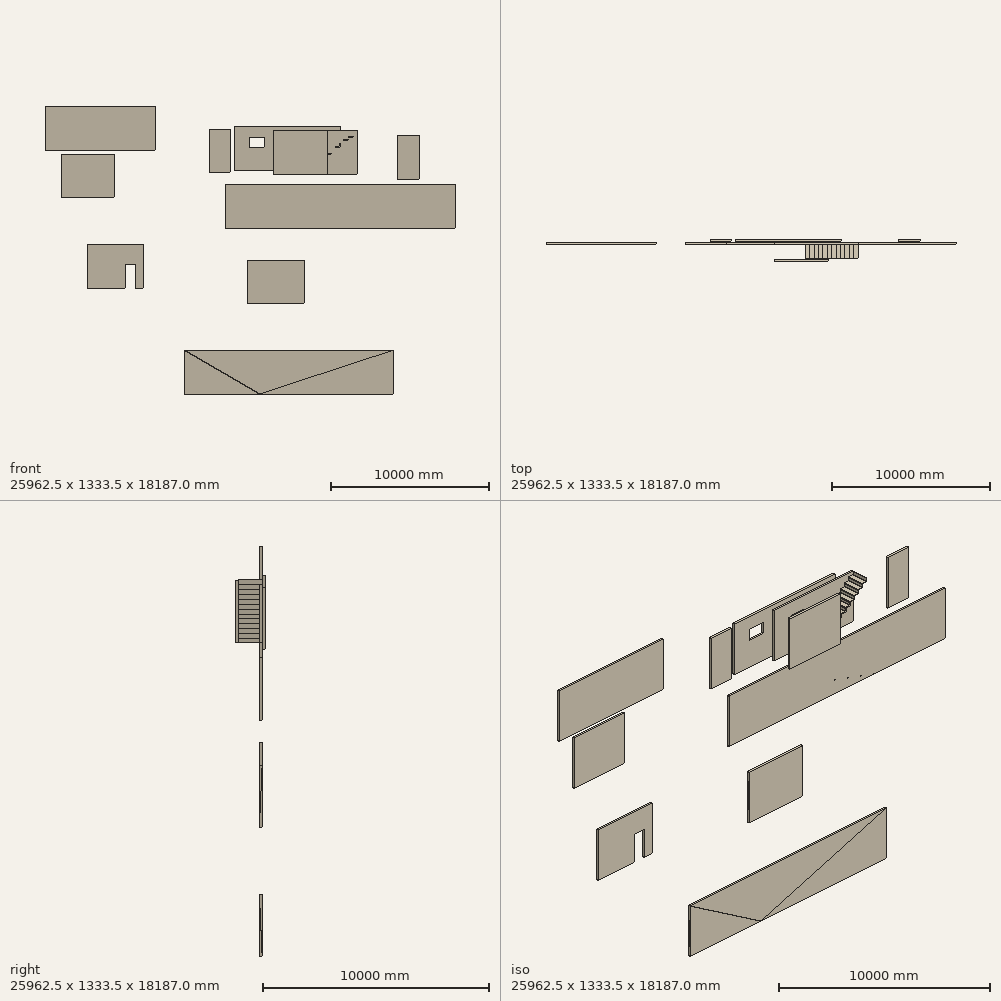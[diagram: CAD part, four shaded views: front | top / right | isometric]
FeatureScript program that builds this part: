
annotation { "Feature Type Name" : "Feature", "Feature Type Description" : "" }
export const myFeature = defineFeature(function(context is Context, id is Id, definition is map)
    precondition{}
    {
        {
            var Q0;
            Q0=qCreatedBy(makeId("Front.planeOp"),FACE);
            var sketch = newSketch(context, id + "F0", { "sketchPlane" : qUnion([Q0])});
            skLineSegment(sketch, "E0", {"start": v(2395.88, -99.39) * mm, "end": v(2414.93, -99.39) * mm});
            skLineSegment(sketch, "E1", {"start": v(2395.88, -99.39) * mm, "end": v(2395.88, -277.19) * mm});
            skLineSegment(sketch, "E2.bottom", {"start": v(2395.88, -277.19) * mm, "end": v(2097.43, -277.19) * mm});
            skLineSegment(sketch, "E2.top", {"start": v(2280.9, -315.29) * mm, "end": v(2135.53, -315.29) * mm});
            skLineSegment(sketch, "E2.right", {"start": v(2097.43, -277.19) * mm, "end": v(2097.43, -315.29) * mm});
            skLineSegment(sketch, "E3", {"start": v(2414.93, -99.39) * mm, "end": v(2414.93, -315.29) * mm});
            skLineSegment(sketch, "E4", {"start": v(2414.93, -315.29) * mm, "end": v(2280.9, -315.29) * mm});
            skLineSegment(sketch, "E5", {"start": v(1837.08, -531.19) * mm, "end": v(1837.08, -708.99) * mm});
            skLineSegment(sketch, "E6.bottom", {"start": v(1837.08, -708.99) * mm, "end": v(1538.63, -708.99) * mm});
            skLineSegment(sketch, "E6.top", {"start": v(1805.95, -747.09) * mm, "end": v(1576.73, -747.09) * mm});
            skLineSegment(sketch, "E6.right", {"start": v(1538.63, -708.99) * mm, "end": v(1538.63, -747.09) * mm});
            skLineSegment(sketch, "E7", {"start": v(1856.13, -531.19) * mm, "end": v(1856.13, -747.09) * mm});
            skLineSegment(sketch, "E8", {"start": v(1856.13, -747.09) * mm, "end": v(1805.95, -747.09) * mm});
            skLineSegment(sketch, "E9", {"start": v(2116.48, -315.29) * mm, "end": v(2116.48, -493.09) * mm});
            skLineSegment(sketch, "E10.bottom", {"start": v(2116.48, -493.09) * mm, "end": v(1818.03, -493.09) * mm});
            skLineSegment(sketch, "E10.top", {"start": v(2135.53, -531.19) * mm, "end": v(1856.13, -531.19) * mm});
            skLineSegment(sketch, "E10.right", {"start": v(1818.03, -493.09) * mm, "end": v(1818.03, -531.19) * mm});
            skLineSegment(sketch, "E11", {"start": v(2135.53, -315.29) * mm, "end": v(2135.53, -531.19) * mm});
            skLineSegment(sketch, "E12", {"start": v(998.88, -1178.89) * mm, "end": v(998.88, -1356.69) * mm});
            skLineSegment(sketch, "E13.bottom", {"start": v(998.88, -1356.69) * mm, "end": v(700.43, -1356.69) * mm});
            skLineSegment(sketch, "E13.top", {"start": v(1017.93, -1394.79) * mm, "end": v(738.53, -1394.79) * mm});
            skLineSegment(sketch, "E13.right", {"start": v(700.43, -1356.69) * mm, "end": v(700.43, -1394.79) * mm});
            skLineSegment(sketch, "E14", {"start": v(1017.93, -1178.89) * mm, "end": v(1017.93, -1394.79) * mm});
            skLineSegment(sketch, "E15", {"start": v(1557.68, -747.09) * mm, "end": v(1557.68, -924.89) * mm});
            skLineSegment(sketch, "E16.bottom", {"start": v(1557.68, -924.89) * mm, "end": v(1259.23, -924.89) * mm});
            skLineSegment(sketch, "E16.top", {"start": v(1557.68, -962.99) * mm, "end": v(1297.33, -962.99) * mm});
            skLineSegment(sketch, "E16.right", {"start": v(1259.23, -924.89) * mm, "end": v(1259.23, -962.99) * mm});
            skLineSegment(sketch, "E17", {"start": v(1576.73, -747.09) * mm, "end": v(1576.73, -962.99) * mm});
            skLineSegment(sketch, "E18", {"start": v(1576.73, -962.99) * mm, "end": v(1557.68, -962.99) * mm});
            skLineSegment(sketch, "E19", {"start": v(1278.28, -962.99) * mm, "end": v(1278.28, -1140.79) * mm});
            skLineSegment(sketch, "E20.bottom", {"start": v(1278.28, -1140.79) * mm, "end": v(979.83, -1140.79) * mm});
            skLineSegment(sketch, "E20.right", {"start": v(979.83, -1140.79) * mm, "end": v(979.83, -1178.89) * mm});
            skLineSegment(sketch, "E21", {"start": v(1297.33, -962.99) * mm, "end": v(1297.33, -1178.89) * mm});
            skLineSegment(sketch, "E22", {"start": v(1297.33, -1178.89) * mm, "end": v(1017.93, -1178.89) * mm});
            skLineSegment(sketch, "E23.bottom", {"start": v(2414.93, -99.39) * mm, "end": v(-2893.67, -99.39) * mm});
            skLineSegment(sketch, "E23.top", {"start": v(2414.93, -2867.99) * mm, "end": v(-2893.67, -2867.99) * mm});
            skLineSegment(sketch, "E23.left", {"start": v(2414.93, -99.39) * mm, "end": v(2414.93, -2867.99) * mm});
            skLineSegment(sketch, "E23.right", {"start": v(-2893.67, -99.39) * mm, "end": v(-2893.67, -2867.99) * mm});
            skLineSegment(sketch, "E24", {"start": v(719.48, -1394.79) * mm, "end": v(719.48, -1572.59) * mm});
            skLineSegment(sketch, "E25.bottom", {"start": v(719.48, -1572.59) * mm, "end": v(421.03, -1572.59) * mm});
            skLineSegment(sketch, "E25.right", {"start": v(421.03, -1572.59) * mm, "end": v(421.03, -1610.69) * mm});
            skLineSegment(sketch, "E26", {"start": v(738.53, -1394.79) * mm, "end": v(738.53, -1610.69) * mm});
            skLineSegment(sketch, "E27", {"start": v(738.53, -1610.69) * mm, "end": v(459.13, -1610.69) * mm});
            skLineSegment(sketch, "E28", {"start": v(160.68, -1826.59) * mm, "end": v(160.68, -2004.39) * mm});
            skLineSegment(sketch, "E29.bottom", {"start": v(160.68, -2004.39) * mm, "end": v(-137.77, -2004.39) * mm});
            skLineSegment(sketch, "E29.top", {"start": v(160.68, -2042.49) * mm, "end": v(-99.67, -2042.49) * mm});
            skLineSegment(sketch, "E29.right", {"start": v(-137.77, -2004.39) * mm, "end": v(-137.77, -2042.49) * mm});
            skLineSegment(sketch, "E30", {"start": v(179.73, -1826.59) * mm, "end": v(179.73, -2042.49) * mm});
            skLineSegment(sketch, "E31", {"start": v(179.73, -2042.49) * mm, "end": v(160.68, -2042.49) * mm});
            skLineSegment(sketch, "E32", {"start": v(440.08, -1610.69) * mm, "end": v(440.08, -1788.49) * mm});
            skLineSegment(sketch, "E33.bottom", {"start": v(440.08, -1788.49) * mm, "end": v(141.63, -1788.49) * mm});
            skLineSegment(sketch, "E33.top", {"start": v(440.08, -1826.59) * mm, "end": v(179.73, -1826.59) * mm});
            skLineSegment(sketch, "E33.right", {"start": v(141.63, -1788.49) * mm, "end": v(141.63, -1826.59) * mm});
            skLineSegment(sketch, "E34", {"start": v(459.13, -1610.69) * mm, "end": v(459.13, -1826.59) * mm});
            skLineSegment(sketch, "E35", {"start": v(459.13, -1826.59) * mm, "end": v(440.08, -1826.59) * mm});
            skLineSegment(sketch, "E36", {"start": v(-118.72, -2042.49) * mm, "end": v(-118.72, -2220.29) * mm});
            skLineSegment(sketch, "E37.bottom", {"start": v(-118.72, -2220.29) * mm, "end": v(-417.17, -2220.29) * mm});
            skLineSegment(sketch, "E37.right", {"start": v(-417.17, -2220.29) * mm, "end": v(-417.17, -2258.39) * mm});
            skLineSegment(sketch, "E38", {"start": v(-99.67, -2042.49) * mm, "end": v(-99.67, -2258.39) * mm});
            skLineSegment(sketch, "E39", {"start": v(-99.67, -2258.39) * mm, "end": v(-379.07, -2258.39) * mm});
            skLineSegment(sketch, "E40", {"start": v(-398.12, -2258.39) * mm, "end": v(-398.12, -2436.19) * mm});
            skLineSegment(sketch, "E41.bottom", {"start": v(-398.12, -2436.19) * mm, "end": v(-696.57, -2436.19) * mm});
            skLineSegment(sketch, "E41.right", {"start": v(-696.57, -2436.19) * mm, "end": v(-696.57, -2474.29) * mm});
            skLineSegment(sketch, "E42", {"start": v(-379.07, -2258.39) * mm, "end": v(-379.07, -2474.29) * mm});
            skLineSegment(sketch, "E43", {"start": v(-379.07, -2474.29) * mm, "end": v(-658.47, -2474.29) * mm});
            skLineSegment(sketch, "E44", {"start": v(-677.52, -2474.29) * mm, "end": v(-677.52, -2652.09) * mm});
            skLineSegment(sketch, "E45.bottom", {"start": v(-677.52, -2652.09) * mm, "end": v(-975.97, -2652.09) * mm});
            skLineSegment(sketch, "E45.right", {"start": v(-975.97, -2652.09) * mm, "end": v(-975.97, -2690.19) * mm});
            skLineSegment(sketch, "E46", {"start": v(-658.47, -2474.29) * mm, "end": v(-658.47, -2690.19) * mm});
            skLineSegment(sketch, "E47", {"start": v(-658.47, -2690.19) * mm, "end": v(-937.87, -2690.19) * mm});
            skLineSegment(sketch, "E48.top", {"start": v(-956.92, -2867.99) * mm, "end": v(-937.87, -2867.99) * mm});
            skLineSegment(sketch, "E48.left", {"start": v(-956.92, -2690.19) * mm, "end": v(-956.92, -2867.99) * mm});
            skLineSegment(sketch, "E48.right", {"start": v(-937.87, -2690.19) * mm, "end": v(-937.87, -2867.99) * mm});
            skLineSegment(sketch, "E49.trimOffspring", {"start": v(2116.48, -315.29) * mm, "end": v(2097.43, -315.29) * mm});
            skLineSegment(sketch, "E50.trimOffspring", {"start": v(1837.08, -531.19) * mm, "end": v(1818.03, -531.19) * mm});
            skLineSegment(sketch, "E51.trimOffspring", {"start": v(1557.68, -747.09) * mm, "end": v(1538.63, -747.09) * mm});
            skLineSegment(sketch, "E52.trimOffspring", {"start": v(1278.28, -962.99) * mm, "end": v(1259.23, -962.99) * mm});
            skLineSegment(sketch, "E53.trimOffspring", {"start": v(998.88, -1178.89) * mm, "end": v(979.83, -1178.89) * mm});
            skLineSegment(sketch, "E54.trimOffspring", {"start": v(719.48, -1394.79) * mm, "end": v(700.43, -1394.79) * mm});
            skLineSegment(sketch, "E55.trimOffspring", {"start": v(440.08, -1610.69) * mm, "end": v(421.03, -1610.69) * mm});
            skLineSegment(sketch, "E56.trimOffspring", {"start": v(160.68, -1826.59) * mm, "end": v(141.63, -1826.59) * mm});
            skLineSegment(sketch, "E57.trimOffspring", {"start": v(-118.72, -2042.49) * mm, "end": v(-137.77, -2042.49) * mm});
            skLineSegment(sketch, "E58.trimOffspring", {"start": v(-398.12, -2258.39) * mm, "end": v(-417.17, -2258.39) * mm});
            skLineSegment(sketch, "E59.trimOffspring", {"start": v(-677.52, -2474.29) * mm, "end": v(-696.57, -2474.29) * mm});
            skLineSegment(sketch, "E60.trimOffspring", {"start": v(-956.92, -2690.19) * mm, "end": v(-975.97, -2690.19) * mm});
            skLineSegment(sketch, "E61.bottom", {"start": v(-1772.9, -816.92) * mm, "end": v(-963.27, -816.92) * mm});
            skLineSegment(sketch, "E61.top", {"start": v(-1772.9, -1394.79) * mm, "end": v(-963.27, -1394.79) * mm});
            skLineSegment(sketch, "E61.left", {"start": v(-1772.9, -816.92) * mm, "end": v(-1772.9, -1394.79) * mm});
            skLineSegment(sketch, "E61.right", {"start": v(-963.27, -816.92) * mm, "end": v(-963.27, -1394.79) * mm});
            skLineSegment(sketch, "E62.bottom", {"start": v(-984.42, -11080.12) * mm, "end": v(-4578.52, -11080.12) * mm});
            skLineSegment(sketch, "E62.top", {"start": v(-984.42, -8311.52) * mm, "end": v(-4578.52, -8311.52) * mm});
            skLineSegment(sketch, "E62.left", {"start": v(-984.42, -11080.12) * mm, "end": v(-984.42, -8311.52) * mm});
            skLineSegment(sketch, "E62.right", {"start": v(-4578.52, -11080.12) * mm, "end": v(-4578.52, -8311.52) * mm});
            skPoint(sketch, "E62.middle", {"position": v(-2781.47, -9695.82) * mm});
            skLineSegment(sketch, "E63.bottom", {"start": v(8601.23, -6325.37) * mm, "end": v(-5942.68, -6325.37) * mm});
            skLineSegment(sketch, "E63.top", {"start": v(8601.23, -3556.77) * mm, "end": v(-5942.68, -3556.77) * mm});
            skLineSegment(sketch, "E63.left", {"start": v(8601.23, -6325.37) * mm, "end": v(8601.23, -3556.77) * mm});
            skLineSegment(sketch, "E63.right", {"start": v(-5942.68, -6325.37) * mm, "end": v(-5942.68, -3556.77) * mm});
            skPoint(sketch, "E63.middle", {"position": v(1329.27, -4941.07) * mm});
            skLineSegment(sketch, "E64.bottom", {"start": v(4653.66, -16802.72) * mm, "end": v(-8547.23, -16802.72) * mm});
            skLineSegment(sketch, "E64.top", {"start": v(4653.66, -14034.12) * mm, "end": v(-8547.23, -14034.12) * mm});
            skLineSegment(sketch, "E64.left", {"start": v(4653.66, -16802.72) * mm, "end": v(4653.66, -14034.12) * mm});
            skLineSegment(sketch, "E64.right", {"start": v(-8547.23, -16802.72) * mm, "end": v(-8547.23, -14034.12) * mm});
            skPoint(sketch, "E64.middle", {"position": v(-1946.79, -15418.42) * mm});
            skLineSegment(sketch, "E65.bottom", {"start": v(-11136.45, -10094.37) * mm, "end": v(-14730.55, -10094.37) * mm});
            skLineSegment(sketch, "E65.top", {"start": v(-11136.45, -7325.77) * mm, "end": v(-14730.55, -7325.77) * mm});
            skLineSegment(sketch, "E65.left", {"start": v(-11136.45, -10094.37) * mm, "end": v(-11136.45, -7325.77) * mm});
            skLineSegment(sketch, "E65.right", {"start": v(-14730.55, -10094.37) * mm, "end": v(-14730.55, -7325.77) * mm});
            skPoint(sketch, "E65.middle", {"position": v(-12933.5, -8710.07) * mm});
            skLineSegment(sketch, "E66.bottom", {"start": v(-10369.88, -1384.3) * mm, "end": v(-17361.23, -1384.3) * mm});
            skLineSegment(sketch, "E66.top", {"start": v(-10369.88, 1384.3) * mm, "end": v(-17361.23, 1384.3) * mm});
            skLineSegment(sketch, "E66.left", {"start": v(-10369.88, -1384.3) * mm, "end": v(-10369.88, 1384.3) * mm});
            skLineSegment(sketch, "E66.right", {"start": v(-17361.23, -1384.3) * mm, "end": v(-17361.23, 1384.3) * mm});
            skPoint(sketch, "E66.middle", {"position": v(-13865.56, 0) * mm});
            skLineSegment(sketch, "E67.bottom", {"start": v(-12994.75, -4376.62) * mm, "end": v(-16357.07, -4376.62) * mm});
            skLineSegment(sketch, "E67.top", {"start": v(-12994.75, -1608.02) * mm, "end": v(-16357.07, -1608.02) * mm});
            skLineSegment(sketch, "E67.left", {"start": v(-12994.75, -4376.62) * mm, "end": v(-12994.75, -1608.02) * mm});
            skLineSegment(sketch, "E67.right", {"start": v(-16357.07, -4376.62) * mm, "end": v(-16357.07, -1608.02) * mm});
            skPoint(sketch, "E67.middle", {"position": v(-14675.91, -2992.32) * mm});
            skCircle(sketch, "E68", {"center": v(-3794.26, -16802.72) * mm, "radius": 3.18 * mm});
            skCircle(sketch, "E69", {"center": v(3848.26, -6325.37) * mm, "radius": 3.18 * mm});
            skLineSegment(sketch, "E70.bottom", {"start": v(-14047.12, -10094.37) * mm, "end": v(-13449.67, -10094.37) * mm});
            skLineSegment(sketch, "E71.bottom", {"start": v(-11648.33, -10094.37) * mm, "end": v(-12317.56, -10094.37) * mm});
            skLineSegment(sketch, "E71.top", {"start": v(-11648.33, -8564.93) * mm, "end": v(-12317.56, -8564.93) * mm});
            skLineSegment(sketch, "E71.left", {"start": v(-11648.33, -10094.37) * mm, "end": v(-11648.33, -8564.93) * mm});
            skLineSegment(sketch, "E71.right", {"start": v(-12317.56, -10094.37) * mm, "end": v(-12317.56, -8564.93) * mm});
            skSolve(sketch);
        }
        {
            var Q0;
            Q0=makeQuery(id+"F0.imprint","IMPRINT",FACE,{"disambiguationData":[TD([[makeQuery(id+"F0.imprint","IMPRINT",EDGE,{"derivedFrom":sQuery(id+"F0.wireOp",EDGE,"E0")}),-1.0]])]});
            extrude(context, id + "F1", {"entities" : qUnion([Q0]), "depth" : 1035.05 * mm, "offsetDistance" : 25.4 * mm});
        }
        {
            var Q0;
            Q0=makeQuery(id+"F1.opExtrude","CAP_FACE",FACE,{"disambiguationData":[OSD([sQuery(id+"F0.wireOp",EDGE,"E0"),sQuery(id+"F0.wireOp",EDGE,"E1"),sQuery(id+"F0.wireOp",EDGE,"E2.bottom"),sQuery(id+"F0.wireOp",EDGE,"E2.top"),sQuery(id+"F0.wireOp",EDGE,"E2.right"),sQuery(id+"F0.wireOp",EDGE,"E3"),sQuery(id+"F0.wireOp",EDGE,"E4"),sQuery(id+"F0.wireOp",EDGE,"E5"),sQuery(id+"F0.wireOp",EDGE,"E6.bottom"),sQuery(id+"F0.wireOp",EDGE,"E6.top"),sQuery(id+"F0.wireOp",EDGE,"E6.right"),sQuery(id+"F0.wireOp",EDGE,"E7"),sQuery(id+"F0.wireOp",EDGE,"E8"),sQuery(id+"F0.wireOp",EDGE,"E9"),sQuery(id+"F0.wireOp",EDGE,"E10.bottom"),sQuery(id+"F0.wireOp",EDGE,"E10.top"),sQuery(id+"F0.wireOp",EDGE,"E10.right"),sQuery(id+"F0.wireOp",EDGE,"E11"),sQuery(id+"F0.wireOp",EDGE,"E12"),sQuery(id+"F0.wireOp",EDGE,"E13.bottom"),sQuery(id+"F0.wireOp",EDGE,"E13.top"),sQuery(id+"F0.wireOp",EDGE,"E13.right"),sQuery(id+"F0.wireOp",EDGE,"E14"),sQuery(id+"F0.wireOp",EDGE,"E15"),sQuery(id+"F0.wireOp",EDGE,"E16.bottom"),sQuery(id+"F0.wireOp",EDGE,"E16.top"),sQuery(id+"F0.wireOp",EDGE,"E16.right"),sQuery(id+"F0.wireOp",EDGE,"E17"),sQuery(id+"F0.wireOp",EDGE,"E18"),sQuery(id+"F0.wireOp",EDGE,"E19"),sQuery(id+"F0.wireOp",EDGE,"E20.bottom"),sQuery(id+"F0.wireOp",EDGE,"E20.right"),sQuery(id+"F0.wireOp",EDGE,"E21"),sQuery(id+"F0.wireOp",EDGE,"E22"),sQuery(id+"F0.wireOp",EDGE,"E23.top"),sQuery(id+"F0.wireOp",EDGE,"E24"),sQuery(id+"F0.wireOp",EDGE,"E25.bottom"),sQuery(id+"F0.wireOp",EDGE,"E25.right"),sQuery(id+"F0.wireOp",EDGE,"E26"),sQuery(id+"F0.wireOp",EDGE,"E27"),sQuery(id+"F0.wireOp",EDGE,"E28"),sQuery(id+"F0.wireOp",EDGE,"E29.bottom"),sQuery(id+"F0.wireOp",EDGE,"E29.top"),sQuery(id+"F0.wireOp",EDGE,"E29.right"),sQuery(id+"F0.wireOp",EDGE,"E30"),sQuery(id+"F0.wireOp",EDGE,"E31"),sQuery(id+"F0.wireOp",EDGE,"E32"),sQuery(id+"F0.wireOp",EDGE,"E33.bottom"),sQuery(id+"F0.wireOp",EDGE,"E33.top"),sQuery(id+"F0.wireOp",EDGE,"E33.right"),sQuery(id+"F0.wireOp",EDGE,"E34"),sQuery(id+"F0.wireOp",EDGE,"E35"),sQuery(id+"F0.wireOp",EDGE,"E36"),sQuery(id+"F0.wireOp",EDGE,"E37.bottom"),sQuery(id+"F0.wireOp",EDGE,"E37.right"),sQuery(id+"F0.wireOp",EDGE,"E38"),sQuery(id+"F0.wireOp",EDGE,"E39"),sQuery(id+"F0.wireOp",EDGE,"E40"),sQuery(id+"F0.wireOp",EDGE,"E41.bottom"),sQuery(id+"F0.wireOp",EDGE,"E41.right"),sQuery(id+"F0.wireOp",EDGE,"E42"),sQuery(id+"F0.wireOp",EDGE,"E43"),sQuery(id+"F0.wireOp",EDGE,"E44"),sQuery(id+"F0.wireOp",EDGE,"E45.bottom"),sQuery(id+"F0.wireOp",EDGE,"E45.right"),sQuery(id+"F0.wireOp",EDGE,"E46"),sQuery(id+"F0.wireOp",EDGE,"E47"),sQuery(id+"F0.wireOp",EDGE,"E48.left"),sQuery(id+"F0.wireOp",EDGE,"E48.right"),sQuery(id+"F0.wireOp",EDGE,"E49.trimOffspring"),sQuery(id+"F0.wireOp",EDGE,"E50.trimOffspring"),sQuery(id+"F0.wireOp",EDGE,"E51.trimOffspring"),sQuery(id+"F0.wireOp",EDGE,"E52.trimOffspring"),sQuery(id+"F0.wireOp",EDGE,"E53.trimOffspring"),sQuery(id+"F0.wireOp",EDGE,"E54.trimOffspring"),sQuery(id+"F0.wireOp",EDGE,"E55.trimOffspring"),sQuery(id+"F0.wireOp",EDGE,"E56.trimOffspring"),sQuery(id+"F0.wireOp",EDGE,"E57.trimOffspring"),sQuery(id+"F0.wireOp",EDGE,"E58.trimOffspring"),sQuery(id+"F0.wireOp",EDGE,"E59.trimOffspring"),sQuery(id+"F0.wireOp",EDGE,"E60.trimOffspring")])],"isStart":false});
            cPlane(context, id + "F2", {"entities" : qUnion([Q0]), "cplaneType" : CPlaneType.OFFSET, "offset" : 25.4 * mm, "width" : 152.4 * mm, "height" : 152.4 * mm});
        }
        {
            var Q0;
            Q0=qCreatedBy(id+"F2.planeOp",FACE);
            var sketch = newSketch(context, id + "F3", { "sketchPlane" : qUnion([Q0])});
            skLineSegment(sketch, "E72.bottom", {"start": v(479.87, -119.53) * mm, "end": v(-2911.03, -119.53) * mm});
            skLineSegment(sketch, "E72.top", {"start": v(479.87, -2888.13) * mm, "end": v(-2911.03, -2888.13) * mm});
            skLineSegment(sketch, "E72.left", {"start": v(479.87, -119.53) * mm, "end": v(479.87, -2888.13) * mm});
            skLineSegment(sketch, "E72.right", {"start": v(-2911.03, -119.53) * mm, "end": v(-2911.03, -2888.13) * mm});
            skSolve(sketch);
        }
        {
            var Q0;
            Q0=makeQuery(id+"F3.imprint","IMPRINT",FACE,{"disambiguationData":[TD([[makeQuery(id+"F3.imprint","IMPRINT",EDGE,{"derivedFrom":sQuery(id+"F3.wireOp",EDGE,"E72.bottom")}),1.0]])]});
            extrude(context, id + "F4", {"entities" : qUnion([Q0]), "depth" : 123.82 * mm, "offsetDistance" : 25.4 * mm});
        }
        {
            var Q0;
            Q0=makeQuery(id+"F1.opExtrude","CAP_FACE",FACE,{"disambiguationData":[OSD([sQuery(id+"F0.wireOp",EDGE,"E0"),sQuery(id+"F0.wireOp",EDGE,"E1"),sQuery(id+"F0.wireOp",EDGE,"E2.bottom"),sQuery(id+"F0.wireOp",EDGE,"E2.top"),sQuery(id+"F0.wireOp",EDGE,"E2.right"),sQuery(id+"F0.wireOp",EDGE,"E3"),sQuery(id+"F0.wireOp",EDGE,"E4"),sQuery(id+"F0.wireOp",EDGE,"E5"),sQuery(id+"F0.wireOp",EDGE,"E6.bottom"),sQuery(id+"F0.wireOp",EDGE,"E6.top"),sQuery(id+"F0.wireOp",EDGE,"E6.right"),sQuery(id+"F0.wireOp",EDGE,"E7"),sQuery(id+"F0.wireOp",EDGE,"E8"),sQuery(id+"F0.wireOp",EDGE,"E9"),sQuery(id+"F0.wireOp",EDGE,"E10.bottom"),sQuery(id+"F0.wireOp",EDGE,"E10.top"),sQuery(id+"F0.wireOp",EDGE,"E10.right"),sQuery(id+"F0.wireOp",EDGE,"E11"),sQuery(id+"F0.wireOp",EDGE,"E12"),sQuery(id+"F0.wireOp",EDGE,"E13.bottom"),sQuery(id+"F0.wireOp",EDGE,"E13.top"),sQuery(id+"F0.wireOp",EDGE,"E13.right"),sQuery(id+"F0.wireOp",EDGE,"E14"),sQuery(id+"F0.wireOp",EDGE,"E15"),sQuery(id+"F0.wireOp",EDGE,"E16.bottom"),sQuery(id+"F0.wireOp",EDGE,"E16.top"),sQuery(id+"F0.wireOp",EDGE,"E16.right"),sQuery(id+"F0.wireOp",EDGE,"E17"),sQuery(id+"F0.wireOp",EDGE,"E18"),sQuery(id+"F0.wireOp",EDGE,"E19"),sQuery(id+"F0.wireOp",EDGE,"E20.bottom"),sQuery(id+"F0.wireOp",EDGE,"E20.right"),sQuery(id+"F0.wireOp",EDGE,"E21"),sQuery(id+"F0.wireOp",EDGE,"E22"),sQuery(id+"F0.wireOp",EDGE,"E23.top"),sQuery(id+"F0.wireOp",EDGE,"E24"),sQuery(id+"F0.wireOp",EDGE,"E25.bottom"),sQuery(id+"F0.wireOp",EDGE,"E25.right"),sQuery(id+"F0.wireOp",EDGE,"E26"),sQuery(id+"F0.wireOp",EDGE,"E27"),sQuery(id+"F0.wireOp",EDGE,"E28"),sQuery(id+"F0.wireOp",EDGE,"E29.bottom"),sQuery(id+"F0.wireOp",EDGE,"E29.top"),sQuery(id+"F0.wireOp",EDGE,"E29.right"),sQuery(id+"F0.wireOp",EDGE,"E30"),sQuery(id+"F0.wireOp",EDGE,"E31"),sQuery(id+"F0.wireOp",EDGE,"E32"),sQuery(id+"F0.wireOp",EDGE,"E33.bottom"),sQuery(id+"F0.wireOp",EDGE,"E33.top"),sQuery(id+"F0.wireOp",EDGE,"E33.right"),sQuery(id+"F0.wireOp",EDGE,"E34"),sQuery(id+"F0.wireOp",EDGE,"E35"),sQuery(id+"F0.wireOp",EDGE,"E36"),sQuery(id+"F0.wireOp",EDGE,"E37.bottom"),sQuery(id+"F0.wireOp",EDGE,"E37.right"),sQuery(id+"F0.wireOp",EDGE,"E38"),sQuery(id+"F0.wireOp",EDGE,"E39"),sQuery(id+"F0.wireOp",EDGE,"E40"),sQuery(id+"F0.wireOp",EDGE,"E41.bottom"),sQuery(id+"F0.wireOp",EDGE,"E41.right"),sQuery(id+"F0.wireOp",EDGE,"E42"),sQuery(id+"F0.wireOp",EDGE,"E43"),sQuery(id+"F0.wireOp",EDGE,"E44"),sQuery(id+"F0.wireOp",EDGE,"E45.bottom"),sQuery(id+"F0.wireOp",EDGE,"E45.right"),sQuery(id+"F0.wireOp",EDGE,"E46"),sQuery(id+"F0.wireOp",EDGE,"E47"),sQuery(id+"F0.wireOp",EDGE,"E48.left"),sQuery(id+"F0.wireOp",EDGE,"E48.right"),sQuery(id+"F0.wireOp",EDGE,"E49.trimOffspring"),sQuery(id+"F0.wireOp",EDGE,"E50.trimOffspring"),sQuery(id+"F0.wireOp",EDGE,"E51.trimOffspring"),sQuery(id+"F0.wireOp",EDGE,"E52.trimOffspring"),sQuery(id+"F0.wireOp",EDGE,"E53.trimOffspring"),sQuery(id+"F0.wireOp",EDGE,"E54.trimOffspring"),sQuery(id+"F0.wireOp",EDGE,"E55.trimOffspring"),sQuery(id+"F0.wireOp",EDGE,"E56.trimOffspring"),sQuery(id+"F0.wireOp",EDGE,"E57.trimOffspring"),sQuery(id+"F0.wireOp",EDGE,"E58.trimOffspring"),sQuery(id+"F0.wireOp",EDGE,"E59.trimOffspring"),sQuery(id+"F0.wireOp",EDGE,"E60.trimOffspring")])],"isStart":true});
            cPlane(context, id + "F5", {"entities" : qUnion([Q0]), "cplaneType" : CPlaneType.OFFSET, "offset" : 25.4 * mm, "width" : 152.4 * mm, "height" : 152.4 * mm});
        }
        {
            var Q0;
            Q0=qCreatedBy(id+"F5.planeOp",FACE);
            var sketch = newSketch(context, id + "F6", { "sketchPlane" : qUnion([Q0])});
            skLineSegment(sketch, "E73.bottom", {"start": v(5415.7, -2649.67) * mm, "end": v(-1339.33, -2649.67) * mm});
            skLineSegment(sketch, "E73.top", {"start": v(5415.7, 118.93) * mm, "end": v(-1339.33, 118.93) * mm});
            skLineSegment(sketch, "E73.left", {"start": v(5415.7, -2649.67) * mm, "end": v(5415.7, 118.93) * mm});
            skLineSegment(sketch, "E73.right", {"start": v(-1339.33, -2649.67) * mm, "end": v(-1339.33, 118.93) * mm});
            skPoint(sketch, "E73.middle", {"position": v(2038.18, -1265.37) * mm});
            skLineSegment(sketch, "E74.bottom", {"start": v(5644.25, -19.65) * mm, "end": v(6987.28, -19.65) * mm});
            skLineSegment(sketch, "E74.top", {"start": v(5644.25, -2788.25) * mm, "end": v(6987.28, -2788.25) * mm});
            skLineSegment(sketch, "E74.left", {"start": v(5644.25, -19.65) * mm, "end": v(5644.25, -2788.25) * mm});
            skLineSegment(sketch, "E74.right", {"start": v(6987.28, -19.65) * mm, "end": v(6987.28, -2788.25) * mm});
            skLineSegment(sketch, "E75.bottom", {"start": v(4450.5, -566.87) * mm, "end": v(3485.3, -566.87) * mm});
            skLineSegment(sketch, "E75.top", {"start": v(4450.5, -1176.47) * mm, "end": v(3485.3, -1176.47) * mm});
            skLineSegment(sketch, "E75.left", {"start": v(4450.5, -566.87) * mm, "end": v(4450.5, -1176.47) * mm});
            skLineSegment(sketch, "E75.right", {"start": v(3485.3, -566.87) * mm, "end": v(3485.3, -1176.47) * mm});
            skCircle(sketch, "E76", {"center": v(-126.48, -2649.67) * mm, "radius": 3.17 * mm});
            skLineSegment(sketch, "E77.bottom", {"start": v(-4906.22, -433.6) * mm, "end": v(-6301.72, -433.6) * mm});
            skLineSegment(sketch, "E77.top", {"start": v(-4906.22, -3202.2) * mm, "end": v(-6301.72, -3202.2) * mm});
            skLineSegment(sketch, "E77.left", {"start": v(-4906.22, -433.6) * mm, "end": v(-4906.22, -3202.2) * mm});
            skLineSegment(sketch, "E77.right", {"start": v(-6301.72, -433.6) * mm, "end": v(-6301.72, -3202.2) * mm});
            skSolve(sketch);
        }
        {
            var Q0;
            Q0=makeQuery(id+"F6.imprint","IMPRINT",FACE,{"disambiguationData":[TD([[makeQuery(id+"F6.imprint","IMPRINT",EDGE,{"derivedFrom":sQuery(id+"F6.wireOp",EDGE,"E73.bottom")}),-1.0]])]});
            extrude(context, id + "F7", {"entities" : qUnion([Q0]), "depth" : 123.82 * mm, "offsetDistance" : 25.4 * mm});
        }
        {
            var Q0;
            Q0=makeQuery(id+"F6.imprint","IMPRINT",FACE,{"disambiguationData":[TD([[makeQuery(id+"F6.imprint","IMPRINT",EDGE,{"derivedFrom":sQuery(id+"F6.wireOp",EDGE,"E74.bottom")}),-1.0]])]});
            extrude(context, id + "F8", {"entities" : qUnion([Q0]), "depth" : 123.82 * mm, "offsetDistance" : 25.4 * mm});
        }
        {
            var Q0;
            Q0=makeQuery(id+"F6.imprint","IMPRINT",FACE,{"disambiguationData":[TD([[makeQuery(id+"F6.imprint","IMPRINT",EDGE,{"derivedFrom":sQuery(id+"F6.wireOp",EDGE,"E77.bottom")}),1.0]])]});
            extrude(context, id + "F9", {"entities" : qUnion([Q0]), "depth" : 123.82 * mm, "offsetDistance" : 25.4 * mm});
        }
        {
            var Q0;
            Q0=makeQuery(id+"F0.imprint","IMPRINT",FACE,{"disambiguationData":[TD([[makeQuery(id+"F0.imprint","IMPRINT",EDGE,{"derivedFrom":sQuery(id+"F0.wireOp",EDGE,"E62.bottom")}),-1.0]])]});
            extrude(context, id + "F10", {"entities" : qUnion([Q0]), "depth" : 123.82 * mm, "offsetDistance" : 25.4 * mm});
        }
        {
            var Q0;
            Q0=makeQuery(id+"F0.imprint","IMPRINT",FACE,{"disambiguationData":[TD([[makeQuery(id+"F0.imprint","IMPRINT",EDGE,{"derivedFrom":sQuery(id+"F0.wireOp",EDGE,"E63.top")}),1.0]])]});
            var Q1;
            Q1=makeQuery(id+"F0.imprint","IMPRINT",FACE,{"disambiguationData":[TD([[makeQuery(id+"F0.imprint","IMPRINT",EDGE,{"derivedFrom":sQuery(id+"F0.wireOp",EDGE,"E64.top")}),1.0]])]});
            extrude(context, id + "F11", {"entities" : qUnion([Q0, Q1]), "depth" : 123.82 * mm, "offsetDistance" : 25.4 * mm});
        }
        {
            var Q0;
            Q0=makeQuery(id+"F0.imprint","IMPRINT",FACE,{"disambiguationData":[TD([[makeQuery(id+"F0.imprint","IMPRINT",EDGE,{"derivedFrom":sQuery(id+"F0.wireOp",EDGE,"E65.top")}),1.0]])]});
            var Q1;
            Q1=makeQuery(id+"F0.imprint","IMPRINT",FACE,{"disambiguationData":[TD([[makeQuery(id+"F0.imprint","IMPRINT",EDGE,{"derivedFrom":sQuery(id+"F0.wireOp",EDGE,"E2.top")}),1.0]])]});
            var Q2;
            Q2=makeQuery(id+"F0.imprint","IMPRINT",FACE,{"disambiguationData":[TD([[makeQuery(id+"F0.imprint","IMPRINT",EDGE,{"derivedFrom":sQuery(id+"F0.wireOp",EDGE,"E66.bottom")}),-1.0]])]});
            var Q3;
            Q3=makeQuery(id+"F0.imprint","IMPRINT",FACE,{"disambiguationData":[TD([[makeQuery(id+"F0.imprint","IMPRINT",EDGE,{"derivedFrom":sQuery(id+"F0.wireOp",EDGE,"E64.top")}),1.0]])]});
            var Q4;
            Q4=makeQuery(id+"F0.imprint","IMPRINT",FACE,{"disambiguationData":[TD([[makeQuery(id+"F0.imprint","IMPRINT",EDGE,{"derivedFrom":sQuery(id+"F0.wireOp",EDGE,"E63.top")}),1.0]])]});
            var Q5;
            Q5=makeQuery(id+"F0.imprint","IMPRINT",FACE,{"disambiguationData":[TD([[makeQuery(id+"F0.imprint","IMPRINT",EDGE,{"derivedFrom":sQuery(id+"F0.wireOp",EDGE,"E1")}),-1.0]])]});
            var Q6;
            Q6=makeQuery(id+"F0.imprint","IMPRINT",FACE,{"disambiguationData":[TD([[makeQuery(id+"F0.imprint","IMPRINT",EDGE,{"derivedFrom":sQuery(id+"F0.wireOp",EDGE,"E0")}),-1.0]])]});
            var Q7;
            Q7=makeQuery(id+"F0.imprint","IMPRINT",FACE,{"disambiguationData":[TD([[makeQuery(id+"F0.imprint","IMPRINT",EDGE,{"derivedFrom":sQuery(id+"F0.wireOp",EDGE,"E62.bottom")}),-1.0]])]});
            var Q8;
            Q8=makeQuery(id+"F0.imprint","IMPRINT",FACE,{"disambiguationData":[TD([[makeQuery(id+"F0.imprint","IMPRINT",EDGE,{"derivedFrom":sQuery(id+"F0.wireOp",EDGE,"E67.bottom")}),-1.0]])]});
            var Q9;
            Q9=makeQuery(id+"F0.imprint","IMPRINT",FACE,{"disambiguationData":[TD([[makeQuery(id+"F0.imprint","IMPRINT",EDGE,{"derivedFrom":sQuery(id+"F0.wireOp",EDGE,"E65.top")}),1.0]])]});
            extrude(context, id + "F12", {"entities" : qUnion([Q0, Q1, Q2, Q3, Q4, Q5, Q6, Q7, Q8, Q9]), "depth" : 123.82 * mm, "offsetDistance" : 25.4 * mm});
        }
        {
            var Q0;
            Q0=makeQuery(id+"F0.imprint","IMPRINT",FACE,{"disambiguationData":[TD([[makeQuery(id+"F0.imprint","IMPRINT",EDGE,{"derivedFrom":sQuery(id+"F0.wireOp",EDGE,"E66.bottom")}),-1.0]])]});
            extrude(context, id + "F13", {"entities" : qUnion([Q0]), "operationType" : NewBodyOperationType.ADD, "depth" : 123.82 * mm, "offsetDistance" : 25.4 * mm});
        }
        {
            var Q0;
            Q0=makeQuery(id+"F0.imprint","IMPRINT",FACE,{"disambiguationData":[TD([[makeQuery(id+"F0.imprint","IMPRINT",EDGE,{"derivedFrom":sQuery(id+"F0.wireOp",EDGE,"E67.bottom")}),-1.0]])]});
            extrude(context, id + "F14", {"entities" : qUnion([Q0]), "operationType" : NewBodyOperationType.ADD, "depth" : 123.82 * mm, "offsetDistance" : 25.4 * mm});
        }
    });
